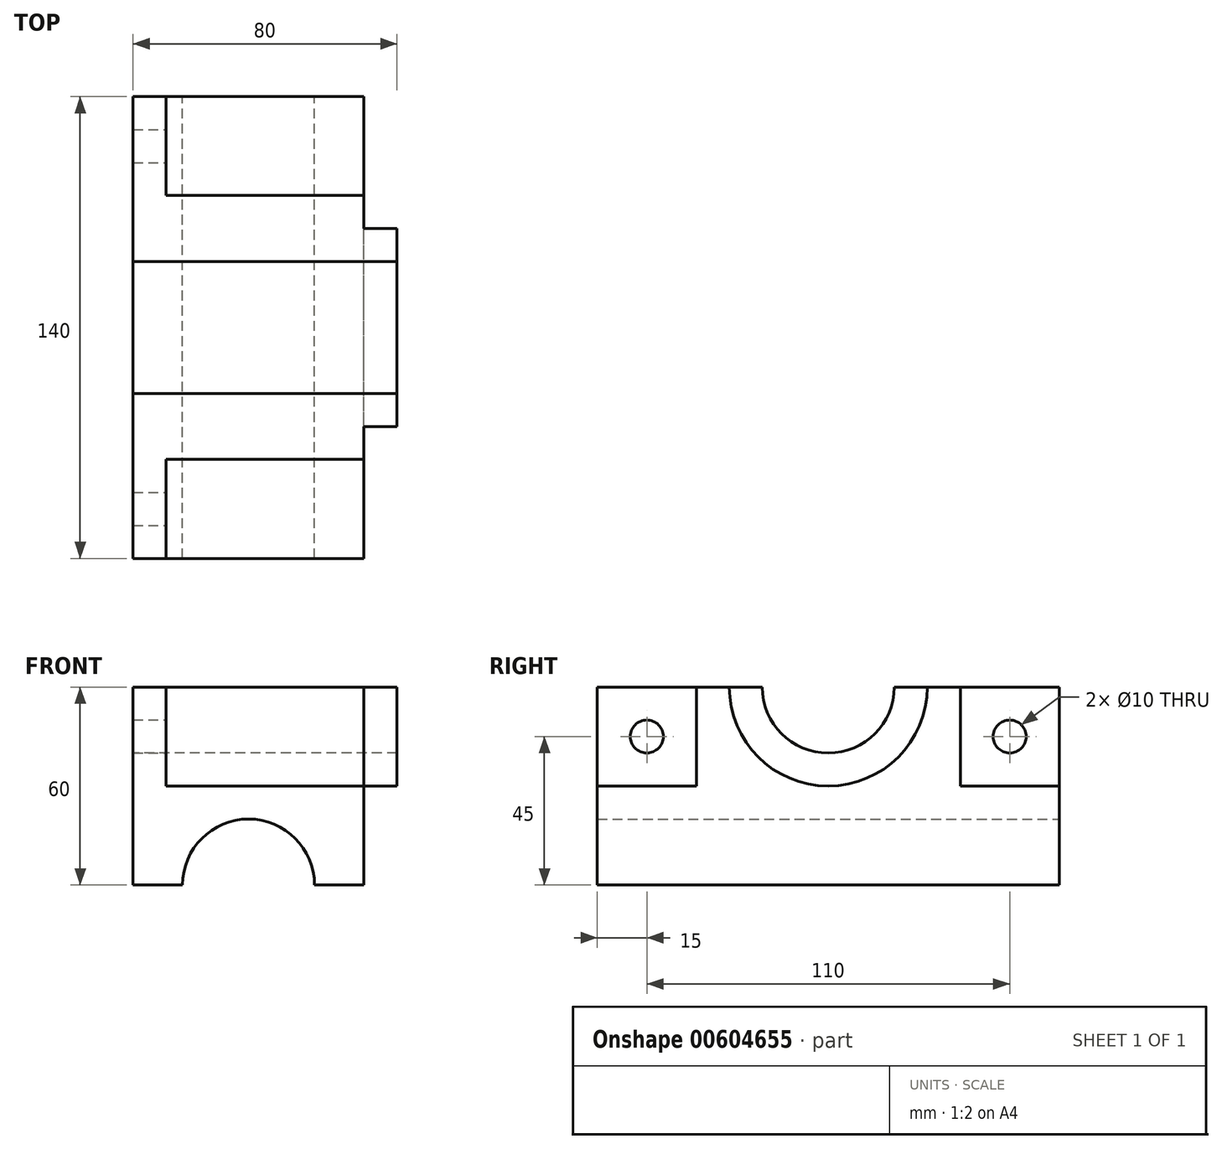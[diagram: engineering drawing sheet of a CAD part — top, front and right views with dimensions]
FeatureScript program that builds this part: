
annotation { "Feature Type Name" : "Feature", "Feature Type Description" : "" }
export const myFeature = defineFeature(function(context is Context, id is Id, definition is map)
    precondition{}
    {
        {
            var Q0;
            Q0=qCreatedBy(makeId("Front.planeOp"),FACE);
            var sketch = newSketch(context, id + "F0", { "sketchPlane" : qUnion([Q0])});
            skLineSegment(sketch, "E0", {"start": v(96.5, 0) * mm, "end": v(81.5, 0) * mm});
            skArc(sketch, "E1", {"start": v(81.5, 0) * mm, "mid": v(61.5, 20) * mm, "end": v(41.5, 0) * mm});
            skLineSegment(sketch, "E2", {"start": v(41.5, 0) * mm, "end": v(26.5, 0) * mm});
            skLineSegment(sketch, "E3", {"start": v(26.5, 0) * mm, "end": v(26.5, 60) * mm});
            skLineSegment(sketch, "E4", {"start": v(26.5, 60) * mm, "end": v(96.5, 60) * mm});
            skLineSegment(sketch, "E5", {"start": v(96.5, 60) * mm, "end": v(96.5, 0) * mm});
            skSolve(sketch);
        }
        {
            var Q0;
            Q0=makeQuery(id+"F0.imprint","IMPRINT",FACE,{"disambiguationData":[TD([[makeQuery(id+"F0.imprint","IMPRINT",EDGE,{"derivedFrom":sQuery(id+"F0.wireOp",EDGE,"E0")}),-1.0]])]});
            extrude(context, id + "F1", {"entities" : qUnion([Q0]), "depth" : 140 * mm, "offsetDistance" : 25 * mm});
        }
        {
            var Q0;
            Q0=makeQuery(id+"F1.opExtrude","SWEPT_FACE",FACE,{"disambiguationData":[OSD([sQuery(id+"F0.wireOp",EDGE,"E4")])]});
            var sketch = newSketch(context, id + "F2", { "sketchPlane" : qUnion([Q0])});
            skLineSegment(sketch, "E6", {"start": v(96.5, 0) * mm, "end": v(96.5, -30) * mm});
            skLineSegment(sketch, "E7", {"start": v(96.5, -30) * mm, "end": v(36.5, -30) * mm});
            skLineSegment(sketch, "E8", {"start": v(36.5, -30) * mm, "end": v(36.5, 0) * mm});
            skSolve(sketch);
        }
        {
            var Q0;
            Q0 = qSketchRegion(id + "F2", true);
            var Q1;
            {var subQ0=sQuery(id+"F2.wireOp",EDGE,"E6");Q1=makeQuery(id+"F2.imprint","IMPRINT",FACE,{"disambiguationData":[TD([[makeQuery(id+"F2.imprint","IMPRINT",EDGE,{"derivedFrom":subQ0}),1.0]])]});}
            extrude(context, id + "F3", {"entities" : qUnion([Q0, Q1]), "operationType" : NewBodyOperationType.REMOVE, "oppositeDirection" : true, "depth" : 30 * mm, "offsetDistance" : 25 * mm});
        }
        {
            var Q0;
            Q0=makeQuery(id+"F3.boolean.opBoolean","COPY",FACE,{"derivedFrom":makeQuery(id+"F3.opExtrude","SWEPT_FACE",FACE,{"disambiguationData":[OSD([sQuery(id+"F2.wireOp",EDGE,"E8")])]})});
            var sketch = newSketch(context, id + "F4", { "sketchPlane" : qUnion([Q0])});
            skCircle(sketch, "E9", {"center": v(-15, 45) * mm, "radius": 5 * mm});
            skSolve(sketch);
        }
        {
            var Q0;
            Q0 = qSketchRegion(id + "F4", true);
            extrude(context, id + "F5", {"entities" : qUnion([Q0]), "operationType" : NewBodyOperationType.REMOVE, "oppositeDirection" : true, "depth" : 10 * mm, "offsetDistance" : 25 * mm});
        }
        {
            var Q0;
            Q0=makeQuery(id+"F1.opExtrude","SWEPT_FACE",FACE,{"disambiguationData":[OSD([sQuery(id+"F0.wireOp",EDGE,"E4")])]});
            var sketch = newSketch(context, id + "F6", { "sketchPlane" : qUnion([Q0])});
            skLineSegment(sketch, "E10", {"start": v(96.5, -140) * mm, "end": v(96.5, -110) * mm});
            skLineSegment(sketch, "E11", {"start": v(96.5, -110) * mm, "end": v(36.5, -110) * mm});
            skLineSegment(sketch, "E12", {"start": v(36.5, -110) * mm, "end": v(36.5, -140) * mm});
            skSolve(sketch);
        }
        {
            var Q0;
            Q0 = qSketchRegion(id + "F6", true);
            var Q1;
            {var subQ0=sQuery(id+"F6.wireOp",EDGE,"E10");Q1=makeQuery(id+"F6.imprint","IMPRINT",FACE,{"disambiguationData":[TD([[makeQuery(id+"F6.imprint","IMPRINT",EDGE,{"derivedFrom":subQ0}),1.0]])]});}
            extrude(context, id + "F7", {"entities" : qUnion([Q0, Q1]), "operationType" : NewBodyOperationType.REMOVE, "oppositeDirection" : true, "depth" : 30 * mm, "offsetDistance" : 25 * mm});
        }
        {
            var Q0;
            Q0=makeQuery(id+"F7.boolean.opBoolean","COPY",FACE,{"derivedFrom":makeQuery(id+"F7.opExtrude","SWEPT_FACE",FACE,{"disambiguationData":[OSD([sQuery(id+"F6.wireOp",EDGE,"E12")])]})});
            var sketch = newSketch(context, id + "F8", { "sketchPlane" : qUnion([Q0])});
            skCircle(sketch, "E13", {"center": v(-125, 45) * mm, "radius": 5 * mm});
            skSolve(sketch);
        }
        {
            var Q0;
            Q0 = qSketchRegion(id + "F8", true);
            extrude(context, id + "F9", {"entities" : qUnion([Q0]), "operationType" : NewBodyOperationType.REMOVE, "oppositeDirection" : true, "depth" : 10 * mm, "offsetDistance" : 25 * mm});
        }
        {
            var Q0;
            Q0=makeQuery(id+"F1.opExtrude","SWEPT_FACE",FACE,{"disambiguationData":[OSD([sQuery(id+"F0.wireOp",EDGE,"E5")])]});
            var sketch = newSketch(context, id + "F10", { "sketchPlane" : qUnion([Q0])});
            skArc(sketch, "E14", {"start": v(-90, 60) * mm, "mid": v(-70, 40) * mm, "end": v(-50, 60) * mm});
            skArc(sketch, "E15", {"start": v(-100, 60) * mm, "mid": v(-70, 30) * mm, "end": v(-40, 60) * mm});
            skLineSegment(sketch, "E16", {"start": v(-100, 60) * mm, "end": v(-90, 60) * mm});
            skLineSegment(sketch, "E17.trimOffspring", {"start": v(-50, 60) * mm, "end": v(-40, 60) * mm});
            skSolve(sketch);
        }
        {
            var Q0;
            Q0=makeQuery(id+"F10.imprint","IMPRINT",FACE,{"disambiguationData":[TD([[makeQuery(id+"F10.imprint","IMPRINT",EDGE,{"derivedFrom":sQuery(id+"F10.wireOp",EDGE,"E14")}),-1.0]])]});
            extrude(context, id + "F11", {"entities" : qUnion([Q0]), "operationType" : NewBodyOperationType.ADD, "depth" : 10 * mm, "offsetDistance" : 25 * mm});
        }
        {
            var Q0;
            Q0=makeQuery(id+"F11.boolean.opBoolean","SPLIT",FACE,{"disambiguationData":[TD([makeQuery(id+"F11.opExtrude","SWEPT_FACE",FACE,{"disambiguationData":[OSD([sQuery(id+"F10.wireOp",EDGE,"E14")])]})])],"derivedFrom":makeQuery(id+"F1.opExtrude","SWEPT_FACE",FACE,{"disambiguationData":[OSD([sQuery(id+"F0.wireOp",EDGE,"E5")])]})});
            extrude(context, id + "F12", {"entities" : qUnion([Q0]), "operationType" : NewBodyOperationType.REMOVE, "oppositeDirection" : true, "depth" : 70 * mm, "offsetDistance" : 25 * mm});
        }
    });
